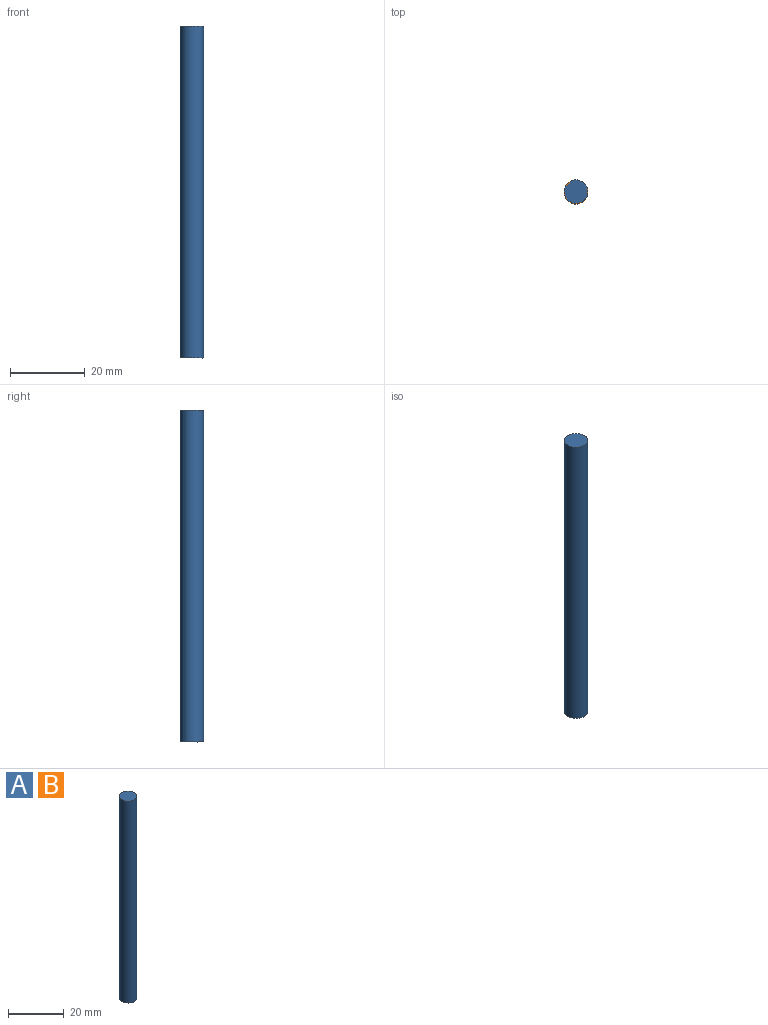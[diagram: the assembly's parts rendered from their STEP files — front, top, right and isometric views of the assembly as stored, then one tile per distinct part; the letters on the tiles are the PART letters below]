
ASSEMBLY  parts=2 mates=1
PART A: 3 faces, bbox 6.4x6.4x88.9 mm
  f0: cylinder r=3.17mm len=88.9mm, axis (0,0,-1), area 1773.5mm2, adj f1,f2
  f1: plane 6.35x6.35mm, normal (0,0,1), area 31.7mm2, adj f0
  f2: plane 6.35x6.35mm, normal (0,0,-1), area 31.7mm2, adj f0
PART B: same geometry as A
PLACE A rot(axis=(0.49,0.84,0.24),0deg) t=(-33.95,9.33,-5.1)mm
PLACE B rot(axis=(0.49,0.84,0.24),0deg) t=(-33.95,9.33,-5.1)mm
MATE fastened B.f0 <-> A.f0  axis (0,0,-1) through (-33.95,9.33,39.35)mm
